# Revit family: RN 55026 Optipress-Therm-Verschlusskappe
name_source: partatom
category: Rohrformteile
units: mm (PartAtom-declared; Revit-internal decimal feet)

## family parameters
Arbeitsebenenbasiert = Nein
Beim Laden mit Abzugskörper schneiden = Nein
Bemaßung runder Anschluss = Durchmesser verwenden
Gemeinsam genutzt = Nein
Immer vertikal = Ja
Teiletyp = Nicht definiert

## types (4) — shared parameters
1.010.00.2 Blattnummer der Richtlinie = 29
1.010.00.3 Ausgabedatum (Monat) der Richtlinie = 201308
1.010.00.4 Herstellername = R. Nussbaum AG
1.010.00.5 Revisionsdatum der Datei = 20190521
1.010.00.6 Webadresse des Herstellers = http://www.nussbaum.ch
1.100.00.4 Produktbezeichnung = Versorgung
1.110.00.2 Index = 1
1.110.00.4 Produktbezeichnung = Optipress-Therm
1.960/3L.00.8 Link (URL) = https://www.nussbaum.ch
29.700.00.4 Produktname = Optipress-Therm-Verschlusskappe, mit Innengewinde exzentrisch
29.700.00.5 Produktkennung = 2
29.700.00.6 Querschnittsform = 1
29.700.00.7 Nennweitensystem = DN
29.700.00.8 Nenndrucksystem = PN
29.710.02.4 Nenndruck = 16
29.710.02.5 max. zul. Überdruck [hPa] = 1600
29.710.02.7 max. zul. Dauer-Betriebsdruck [hPa] = 1600
29.710.02.9 max. zul. Dauer-Betriebstemperatur [°C] = 95
CONNECTOR1_DIAMETER_dX_0r = 20 mm
Connector Visibility = Nein
EnclosingSpace Visibility = Nein
Hersteller = R. Nussbaum AG

## per-type parameters (varying)
| type | 1.800.00.3 TGA-Nummer | 1.800.00.4 Kommentarfeld | 1.810.00.3 Hersteller-Bestellnummer | 1.810.00.4 DATANORM-Nummer | 1.810.00.5 StLB-Nummer | 1.810.00.6 GTIN-Nummer | 29.710.02.10 Formstück-Gewicht [kg] | 29.710.02.3 Benennung | CONNECTOR0_DIAMETER_dX_0r | CONNECTOR0_dX_01 | CONNECTOR0_ref_dX | CONNECTOR1_dX_00 | CONNECTOR1_dX_01 | CONNECTOR1_ref_dX | CONNECTOR1_ref_dZ | Modell | R. Nussbaum AG 55026.70 de Visibility | R. Nussbaum AG 55026.71 de Visibility | R. Nussbaum AG 55026.72 de Visibility | R. Nussbaum AG 55026.73 de Visibility | Typenkommentare |
| DN=60 | 01900100000000000000000000000000000000000000000017000000000000000004 | 55026.70, Optipress-Therm-Verschlusskappe, mit Innengewinde exzentrisch, DN=60, L=99, Rp=¾ | 55026.7 | 55026.70 | 257.554 | 7612945674784 | 0.357 | Optipress-Therm-Verschlusskappe, mit Innengewinde exzentrisch, DN=60, L=99, Rp=¾ | 60 mm | 43 mm  [stored 0.141076 ft] | 43 mm  [stored 0.141076 ft] | 89 mm | 99 mm | 89 mm | 8 mm  [stored 0.0262467 ft] | 55026.7 | Ja | Nein | Nein | Nein | Optipress-Therm-Verschlusskappe DN=60 |
| DN=100 | 01900100000000000000000000000000000000000000000017000000000000000003 | 55026.73, Optipress-Therm-Verschlusskappe, mit Innengewinde exzentrisch, DN=100, L=115, Rp=¾ | 55026.73 | 55026.73 | 257.553 | 7612945674913 | 0.721 | Optipress-Therm-Verschlusskappe, mit Innengewinde exzentrisch, DN=100, L=115, Rp=¾ | 100 mm | 60 mm | 60 mm | 105 mm | 115 mm | 105 mm | 29 mm | 55026.73 | Nein | Nein | Nein | Ja | Optipress-Therm-Verschlusskappe DN=100 |
| DN=80 | 01900100000000000000000000000000000000000000000017000000000000000002 | 55026.72, Optipress-Therm-Verschlusskappe, mit Innengewinde exzentrisch, DN=80, L=105, Rp=¾ | 55026.72 | 55026.72 | 257.552 | 7612945674906 | 0.538 | Optipress-Therm-Verschlusskappe, mit Innengewinde exzentrisch, DN=80, L=105, Rp=¾ | 80 mm | 50 mm | 50 mm | 95 mm | 105 mm | 95 mm | 20 mm | 55026.72 | Nein | Nein | Ja | Nein | Optipress-Therm-Verschlusskappe DN=80 |
| DN=65 | 01900100000000000000000000000000000000000000000017000000000000000001 | 55026.71, Optipress-Therm-Verschlusskappe, mit Innengewinde exzentrisch, DN=65, L=105, Rp=¾ | 55026.71 | 55026.71 | 257.551 | 7612945674791 | 0.444 | Optipress-Therm-Verschlusskappe, mit Innengewinde exzentrisch, DN=65, L=105, Rp=¾ | 65 mm | 50 mm | 50 mm | 95 mm | 105 mm | 95 mm | 14 mm  [stored 0.0459318 ft] | 55026.71 | Nein | Ja | Nein | Nein | Optipress-Therm-Verschlusskappe DN=65 |

note: [stored X ft] marks values corroborated as IEEE doubles in the binary element streams (Revit-internal decimal feet)
